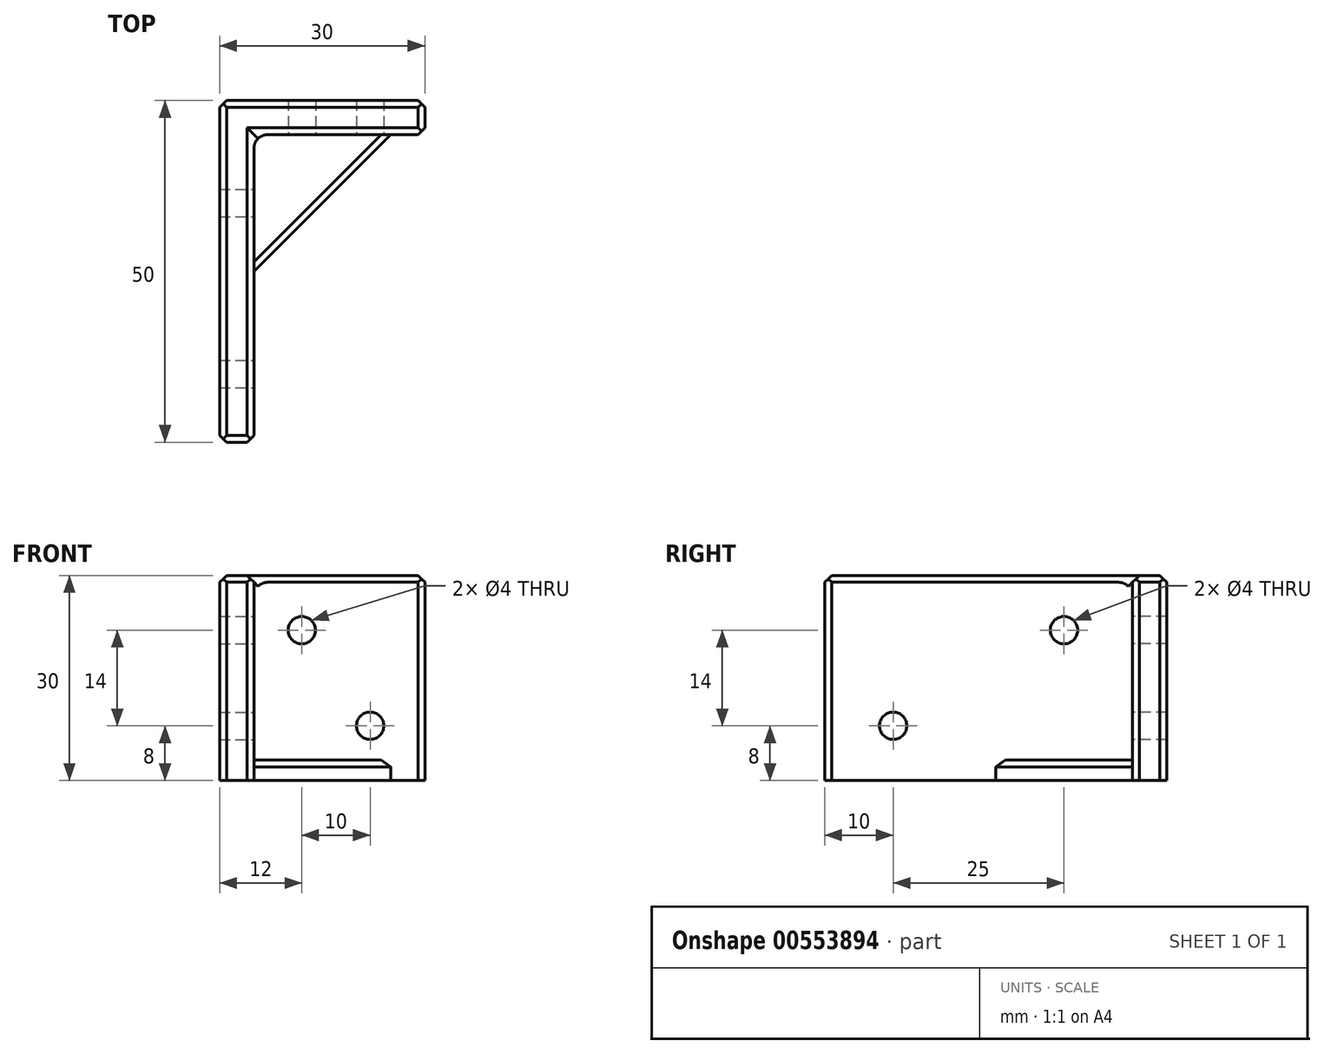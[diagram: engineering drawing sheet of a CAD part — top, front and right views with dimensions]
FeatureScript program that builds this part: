
annotation { "Feature Type Name" : "Feature", "Feature Type Description" : "" }
export const myFeature = defineFeature(function(context is Context, id is Id, definition is map)
    precondition{}
    {
        {
            var Q0;
            Q0=qCreatedBy(makeId("Top.planeOp"),FACE);
            var sketch = newSketch(context, id + "F0", { "sketchPlane" : qUnion([Q0])});
            skLineSegment(sketch, "E0", {"start": v(0, 0) * mm, "end": v(0, 45) * mm});
            skLineSegment(sketch, "E1", {"start": v(0, 45) * mm, "end": v(25, 45) * mm});
            skLineSegment(sketch, "E2", {"start": v(25, 45) * mm, "end": v(25, 50) * mm});
            skLineSegment(sketch, "E3", {"start": v(25, 50) * mm, "end": v(-5, 50) * mm});
            skLineSegment(sketch, "E4", {"start": v(-5, 50) * mm, "end": v(-5, 0) * mm});
            skLineSegment(sketch, "E5", {"start": v(-5, 0) * mm, "end": v(0, 0) * mm});
            skSolve(sketch);
        }
        {
            var Q0;
            Q0 = qSketchRegion(id + "F0", true);
            extrude(context, id + "F1", {"entities" : qUnion([Q0]), "depth" : 30 * mm, "offsetDistance" : 25 * mm});
        }
        {
            var Q0;
            Q0=makeQuery(id+"F1.opExtrude","SWEPT_FACE",FACE,{"disambiguationData":[OSD([sQuery(id+"F0.wireOp",EDGE,"E1")])]});
            var sketch = newSketch(context, id + "F2", { "sketchPlane" : qUnion([Q0])});
            skCircle(sketch, "E6", {"center": v(17, 8) * mm, "radius": 2 * mm});
            skCircle(sketch, "E7", {"center": v(7, 22) * mm, "radius": 2 * mm});
            skSolve(sketch);
        }
        {
            var Q0;
            Q0=makeQuery(id+"F2.imprint","IMPRINT",FACE,{"disambiguationData":[TD([[makeQuery(id+"F2.imprint","IMPRINT",EDGE,{"derivedFrom":sQuery(id+"F2.wireOp",EDGE,"E7")}),1.0]])]});
            var Q1;
            Q1=makeQuery(id+"F2.imprint","IMPRINT",FACE,{"disambiguationData":[TD([[makeQuery(id+"F2.imprint","IMPRINT",EDGE,{"derivedFrom":sQuery(id+"F2.wireOp",EDGE,"E6")}),1.0]])]});
            extrude(context, id + "F3", {"entities" : qUnion([Q0, Q1]), "operationType" : NewBodyOperationType.REMOVE, "oppositeDirection" : true, "depth" : 25 * mm, "offsetDistance" : 25 * mm});
        }
        {
            var Q0;
            Q0=makeQuery(id+"F1.opExtrude","CAP_FACE",FACE,{"disambiguationData":[OSD([sQuery(id+"F0.wireOp",EDGE,"E0"),sQuery(id+"F0.wireOp",EDGE,"E1"),sQuery(id+"F0.wireOp",EDGE,"E2"),sQuery(id+"F0.wireOp",EDGE,"E3"),sQuery(id+"F0.wireOp",EDGE,"E4"),sQuery(id+"F0.wireOp",EDGE,"E5")])],"isStart":false});
            chamfer(context, id + "F4", {"entities" : qUnion([Q0]), "width" : 1 * mm, "tangentPropagation" : true});
        }
        {
            var Q0;
            Q0=makeQuery(id+"F1.opExtrude","SWEPT_FACE",FACE,{"disambiguationData":[OSD([sQuery(id+"F0.wireOp",EDGE,"E0")])]});
            var sketch = newSketch(context, id + "F5", { "sketchPlane" : qUnion([Q0])});
            skCircle(sketch, "E8", {"center": v(10, 8) * mm, "radius": 2 * mm});
            skCircle(sketch, "E9", {"center": v(35, 22) * mm, "radius": 2 * mm});
            skSolve(sketch);
        }
        {
            var Q0;
            Q0=makeQuery(id+"F5.imprint","IMPRINT",FACE,{"disambiguationData":[TD([[makeQuery(id+"F5.imprint","IMPRINT",EDGE,{"derivedFrom":sQuery(id+"F5.wireOp",EDGE,"E9")}),1.0]])]});
            var Q1;
            Q1=makeQuery(id+"F5.imprint","IMPRINT",FACE,{"disambiguationData":[TD([[makeQuery(id+"F5.imprint","IMPRINT",EDGE,{"derivedFrom":sQuery(id+"F5.wireOp",EDGE,"E8")}),1.0]])]});
            extrude(context, id + "F6", {"entities" : qUnion([Q0, Q1]), "operationType" : NewBodyOperationType.REMOVE, "oppositeDirection" : true, "depth" : 25 * mm, "offsetDistance" : 25 * mm});
        }
        {
            var Q0;
            Q0=makeQuery(id+"F1.opExtrude","SWEPT_EDGE",EDGE,{"disambiguationData":[OSD([sQuery(id+"F0.wireOp",EDGE,"E0"),sQuery(id+"F0.wireOp",EDGE,"E5")])]});
            var Q1;
            Q1=makeQuery(id+"F1.opExtrude","SWEPT_EDGE",EDGE,{"disambiguationData":[OSD([sQuery(id+"F0.wireOp",EDGE,"E4"),sQuery(id+"F0.wireOp",EDGE,"E5")])]});
            var Q2;
            Q2=makeQuery(id+"F1.opExtrude","SWEPT_EDGE",EDGE,{"disambiguationData":[OSD([sQuery(id+"F0.wireOp",EDGE,"E1"),sQuery(id+"F0.wireOp",EDGE,"E2")])]});
            var Q3;
            Q3=makeQuery(id+"F1.opExtrude","SWEPT_EDGE",EDGE,{"disambiguationData":[OSD([sQuery(id+"F0.wireOp",EDGE,"E2"),sQuery(id+"F0.wireOp",EDGE,"E3")])]});
            var Q4;
            Q4=makeQuery(id+"F1.opExtrude","SWEPT_EDGE",EDGE,{"disambiguationData":[OSD([sQuery(id+"F0.wireOp",EDGE,"E3"),sQuery(id+"F0.wireOp",EDGE,"E4")])]});
            chamfer(context, id + "F7", {"entities" : qUnion([Q0, Q1, Q2, Q3, Q4]), "width" : 1 * mm, "tangentPropagation" : true});
        }
        {
            var Q0;
            Q0=makeQuery(id+"F1.opExtrude","SWEPT_EDGE",EDGE,{"disambiguationData":[OSD([sQuery(id+"F0.wireOp",EDGE,"E0"),sQuery(id+"F0.wireOp",EDGE,"E1")])]});
            fillet(context, id + "F8", {"entities" : qUnion([Q0]), "radius" : 2 * mm, "tangentPropagation" : true, "allowEdgeOverflow" : false});
        }
        {
            var Q0;
            Q0=makeQuery(id+"F1.opExtrude","CAP_FACE",FACE,{"disambiguationData":[OSD([sQuery(id+"F0.wireOp",EDGE,"E0"),sQuery(id+"F0.wireOp",EDGE,"E1"),sQuery(id+"F0.wireOp",EDGE,"E2"),sQuery(id+"F0.wireOp",EDGE,"E3"),sQuery(id+"F0.wireOp",EDGE,"E4"),sQuery(id+"F0.wireOp",EDGE,"E5")])],"isStart":true});
            var sketch = newSketch(context, id + "F9", { "sketchPlane" : qUnion([Q0])});
            skLineSegment(sketch, "E10.0", {"start": v(0, -25) * mm, "end": v(0, -45) * mm});
            skLineSegment(sketch, "E11.0", {"start": v(0, -45) * mm, "end": v(20, -45) * mm});
            skLineSegment(sketch, "E12", {"start": v(20, -45) * mm, "end": v(0, -25) * mm});
            skPoint(sketch, "E13.orphan", {"position": v(0, -1) * mm});
            skPoint(sketch, "E14.orphan", {"position": v(24, -45) * mm});
            skSolve(sketch);
        }
        {
            var Q0;
            Q0 = qSketchRegion(id + "F9", true);
            extrude(context, id + "F10", {"entities" : qUnion([Q0]), "operationType" : NewBodyOperationType.ADD, "oppositeDirection" : true, "depth" : 3 * mm, "offsetDistance" : 25 * mm});
        }
        {
            var Q0;
            Q0=makeQuery(id+"F10.opExtrude","CAP_EDGE",EDGE,{"disambiguationData":[OSD([sQuery(id+"F9.wireOp",EDGE,"E12")])],"isStart":false});
            chamfer(context, id + "F11", {"entities" : qUnion([Q0]), "width" : 1 * mm, "tangentPropagation" : true});
        }
    });
